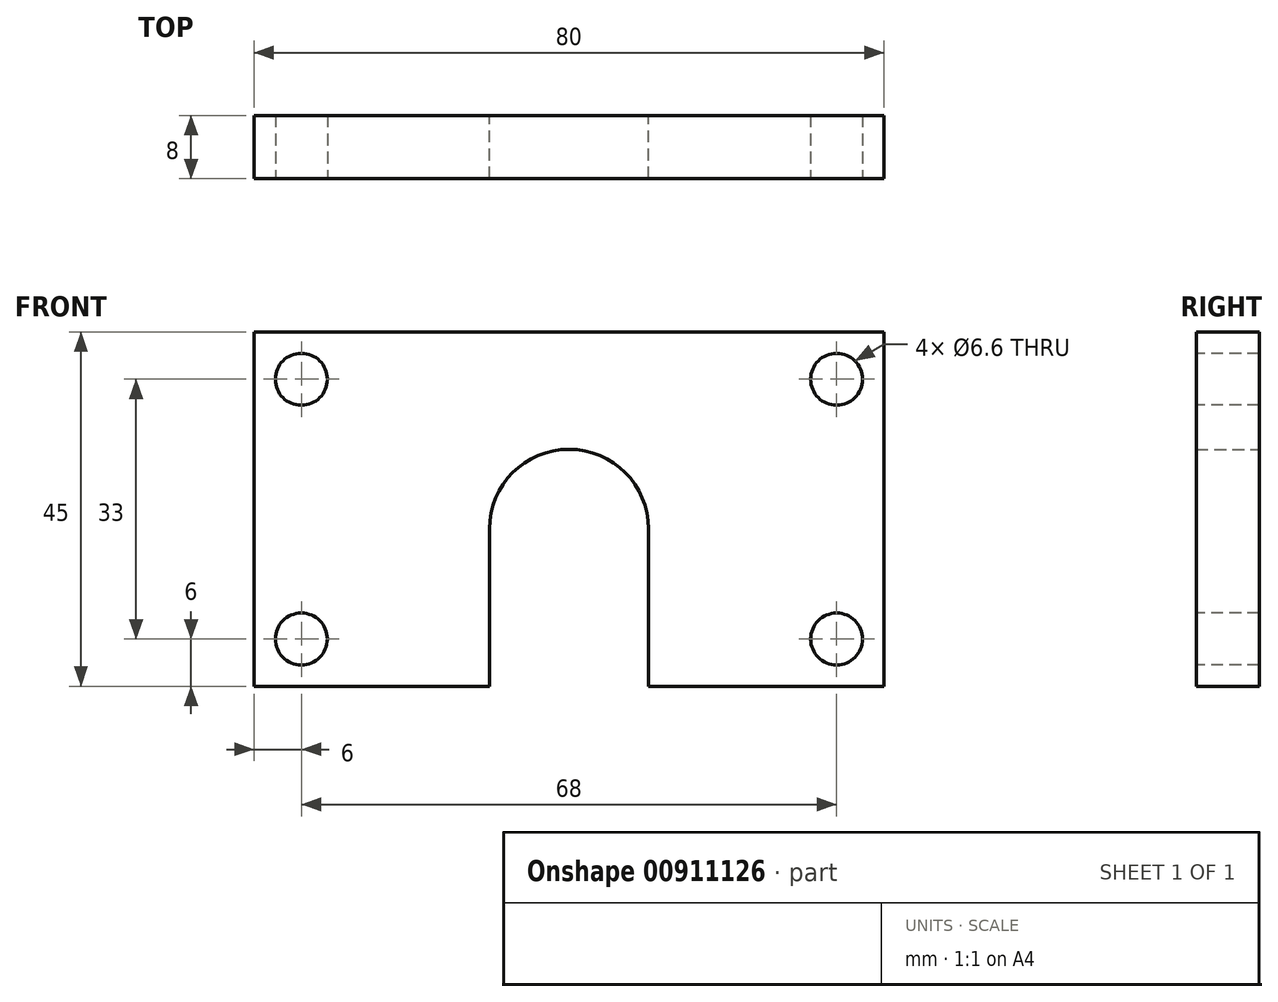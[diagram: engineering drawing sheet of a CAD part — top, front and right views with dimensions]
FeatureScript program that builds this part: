
annotation { "Feature Type Name" : "Feature", "Feature Type Description" : "" }
export const myFeature = defineFeature(function(context is Context, id is Id, definition is map)
    precondition{}
    {
        {
            var Q0;
            Q0=qCreatedBy(makeId("Front.planeOp"),FACE);
            var sketch = newSketch(context, id + "F0", { "sketchPlane" : qUnion([Q0])});
            skLineSegment(sketch, "E0.bottom", {"start": v(-40, 22.5) * mm, "end": v(40, 22.5) * mm});
            skLineSegment(sketch, "E0.top", {"start": v(-40, -22.5) * mm, "end": v(-10.1, -22.5) * mm});
            skLineSegment(sketch, "E0.left", {"start": v(-40, 22.5) * mm, "end": v(-40, -22.5) * mm});
            skLineSegment(sketch, "E0.right", {"start": v(40, 22.5) * mm, "end": v(40, -22.5) * mm});
            skLineSegment(sketch, "E1", {"start": v(-10.1, -2.5) * mm, "end": v(-10.1, -22.5) * mm});
            skLineSegment(sketch, "E2", {"start": v(10.1, -2.5) * mm, "end": v(10.1, -22.5) * mm});
            skLineSegment(sketch, "E3.trimOffspring", {"start": v(10.1, -22.5) * mm, "end": v(40, -22.5) * mm});
            skArc(sketch, "E4", {"start": v(10.1, -2.5) * mm, "mid": v(0, 7.6) * mm, "end": v(-10.1, -2.5) * mm});
            skSolve(sketch);
        }
        {
            var Q0;
            Q0=makeQuery(id+"F0.imprint","IMPRINT",FACE,{"disambiguationData":[TD([[makeQuery(id+"F0.imprint","IMPRINT",EDGE,{"derivedFrom":sQuery(id+"F0.wireOp",EDGE,"E0.bottom")}),-1.0]])]});
            extrude(context, id + "F1", {"entities" : qUnion([Q0]), "depth" : 8 * mm, "offsetDistance" : 25 * mm});
        }
        {
            var Q0;
            Q0=makeQuery(id+"F1.opExtrude","CAP_FACE",FACE,{"disambiguationData":[OSD([sQuery(id+"F0.wireOp",EDGE,"E0.bottom"),sQuery(id+"F0.wireOp",EDGE,"E0.top"),sQuery(id+"F0.wireOp",EDGE,"E0.left"),sQuery(id+"F0.wireOp",EDGE,"E0.right"),sQuery(id+"F0.wireOp",EDGE,"E1"),sQuery(id+"F0.wireOp",EDGE,"E2"),sQuery(id+"F0.wireOp",EDGE,"E3.trimOffspring"),sQuery(id+"F0.wireOp",EDGE,"E4")])],"isStart":false});
            var sketch = newSketch(context, id + "F2", { "sketchPlane" : qUnion([Q0])});
            skCircle(sketch, "E5", {"center": v(34, 16.5) * mm, "radius": 3 * mm});
            skCircle(sketch, "E6.MirrorC", {"center": v(34, -16.5) * mm, "radius": 3 * mm});
            skCircle(sketch, "E7.MirrorC", {"center": v(-34, 16.5) * mm, "radius": 3 * mm});
            skCircle(sketch, "E8.MirrorC", {"center": v(-34, -16.5) * mm, "radius": 3 * mm});
            skSolve(sketch);
        }
        {
            var Q0;
            Q0=sQuery(id+"F2.wireOp",VERTEX,"E7.MirrorC.center");
            var Q1;
            Q1=sQuery(id+"F2.wireOp",VERTEX,"E8.MirrorC.center");
            var Q2;
            Q2=sQuery(id+"F2.wireOp",VERTEX,"E6.MirrorC.center");
            var Q3;
            Q3=sQuery(id+"F2.wireOp",VERTEX,"E5.center");
            var Q4;
            Q4=makeQuery(id+"F1.opExtrude","SWEPT_BODY",BODY,{"disambiguationData":[OSD([sQuery(id+"F0.wireOp",EDGE,"E0.bottom"),sQuery(id+"F0.wireOp",EDGE,"E0.top"),sQuery(id+"F0.wireOp",EDGE,"E0.left"),sQuery(id+"F0.wireOp",EDGE,"E0.right"),sQuery(id+"F0.wireOp",EDGE,"E1"),sQuery(id+"F0.wireOp",EDGE,"E2"),sQuery(id+"F0.wireOp",EDGE,"E3.trimOffspring"),sQuery(id+"F0.wireOp",EDGE,"E4")])]});
            hole(context, id + "F3", {"style" : HoleStyle.SIMPLE, "endStyle" : HoleEndStyle.THROUGH, "standardTappedOrClearance" : lookupTablePath({ "fit" : "Normal", "standard" : "ISO", "size" : "M6", "type" : "Clearance" }), "standardBlindInLast" : lookupTablePath({ "fit" : "Normal", "standard" : "ISO", "size" : "M6", "type" : "Clearance" }), "holeDiameter" : 6.6 * mm, "majorDiameter" : 5 * mm, "isTappedThrough" : true, "tappedDepth" : 12 * mm, "tapClearance" : 3, "locations" : qUnion([Q0, Q1, Q2, Q3]), "scope" : qUnion([Q4])});
        }
    });
